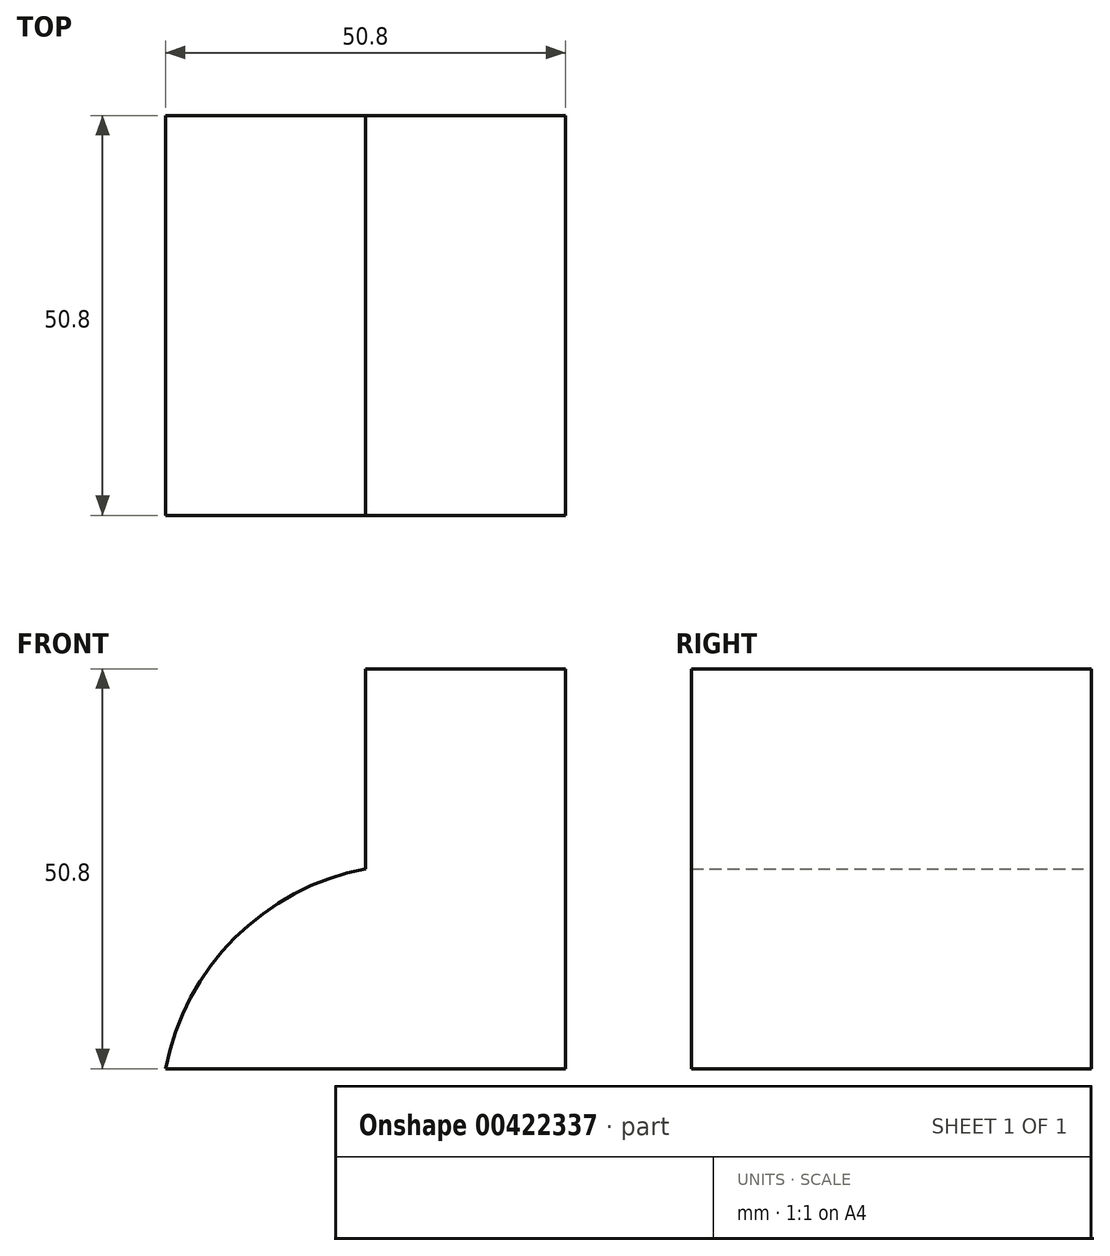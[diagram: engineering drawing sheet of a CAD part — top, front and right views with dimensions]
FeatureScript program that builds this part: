
annotation { "Feature Type Name" : "Feature", "Feature Type Description" : "" }
export const myFeature = defineFeature(function(context is Context, id is Id, definition is map)
    precondition{}
    {
        {
            var Q0;
            Q0=qCreatedBy(makeId("Front.planeOp"),FACE);
            var sketch = newSketch(context, id + "F0", { "sketchPlane" : qUnion([Q0])});
            skLineSegment(sketch, "E0", {"start": v(0, 0) * mm, "end": v(-50.8, 0) * mm});
            skLineSegment(sketch, "E1", {"start": v(0, 0) * mm, "end": v(0, 50.8) * mm});
            skLineSegment(sketch, "E2", {"start": v(0, 50.8) * mm, "end": v(-25.4, 50.8) * mm});
            skLineSegment(sketch, "E3", {"start": v(-25.4, 50.8) * mm, "end": v(-25.4, 25.4) * mm});
            skArc(sketch, "E4", {"start": v(-25.4, 25.4) * mm, "mid": v(-42, 16.6) * mm, "end": v(-50.8, 0) * mm});
            skSolve(sketch);
        }
        {
            var Q0;
            Q0 = qSketchRegion(id + "F0", true);
            extrude(context, id + "F1", {"entities" : qUnion([Q0]), "depth" : 50.8 * mm});
        }
    });
